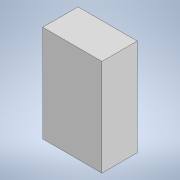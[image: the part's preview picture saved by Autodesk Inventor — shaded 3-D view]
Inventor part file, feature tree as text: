
AUTODESK INVENTOR PART (.ipt)
format: ipt  version: 2021 (Build 250183000, 183)  size: 87,552 bytes
history: native  units: in
note: dims shown in document units (in); Inventor stores cm internally (conversion verified against a paired STEP export)
features: extrude x1, sketch x1
ambient origin geometry x8: Origin, YZ Plane, XZ Plane, XY Plane, X Axis, Y Axis, Z Axis, Center Point
bodies: Solid1 (feature_tree)
feature tree (2):
  extrude  "Extrusion1"  Depth=6.5in
  sketch  "Sketch1"  dims[d0=10.625in d1=6.5in d2=3.875in d3=0.0in]
